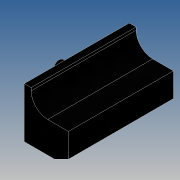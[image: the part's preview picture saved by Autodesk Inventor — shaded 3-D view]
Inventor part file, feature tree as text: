
AUTODESK INVENTOR PART (.ipt)
format: ipt  version: 2016 (Build 200138000, 138)  size: 138,240 bytes
history: native  units: mm
features: extrude x4, sketch x4, fillet x1
ambient origin geometry x8: Origin, YZ Plane, XZ Plane, XY Plane, X Axis, Y Axis, Z Axis, Center Point
bodies: Solid1 (feature_tree)
feature tree (9):
  extrude  "Extrusion1"  Depth=11.2mm
  fillet  "Fillet1"  Radius=2.5mm
  extrude  "Extrusion2"  Depth=5.0mm
  extrude  "Extrusion3"  Depth=38.0mm TaperAngle=0.0deg
  extrude  "Extrusion4"  Depth=2.0mm
  sketch  "Sketch2"  dims[d0=18.2mm d1=11.2mm d2=2.5mm]
  sketch  "Sketch3"  dims[d3=16.0mm d4=5.0mm]
  sketch  "Sketch4"  dims[d5=2.5mm d6=38.0mm d7=0.0mm]
  sketch  "Sketch5"  dims[d8=6.0mm d9=2.0mm d10=33.8mm d11=6.5mm d12=10.0mm d13=0.0mm d14=4.0mm d15=11.0mm d16=6.4mm d17=0.0mm d18=2.0mm d19=5.0mm d20=2.0mm d21=2.5mm d22=1.0mm d23=1.8mm d24=6.4mm d25=0.0mm]
